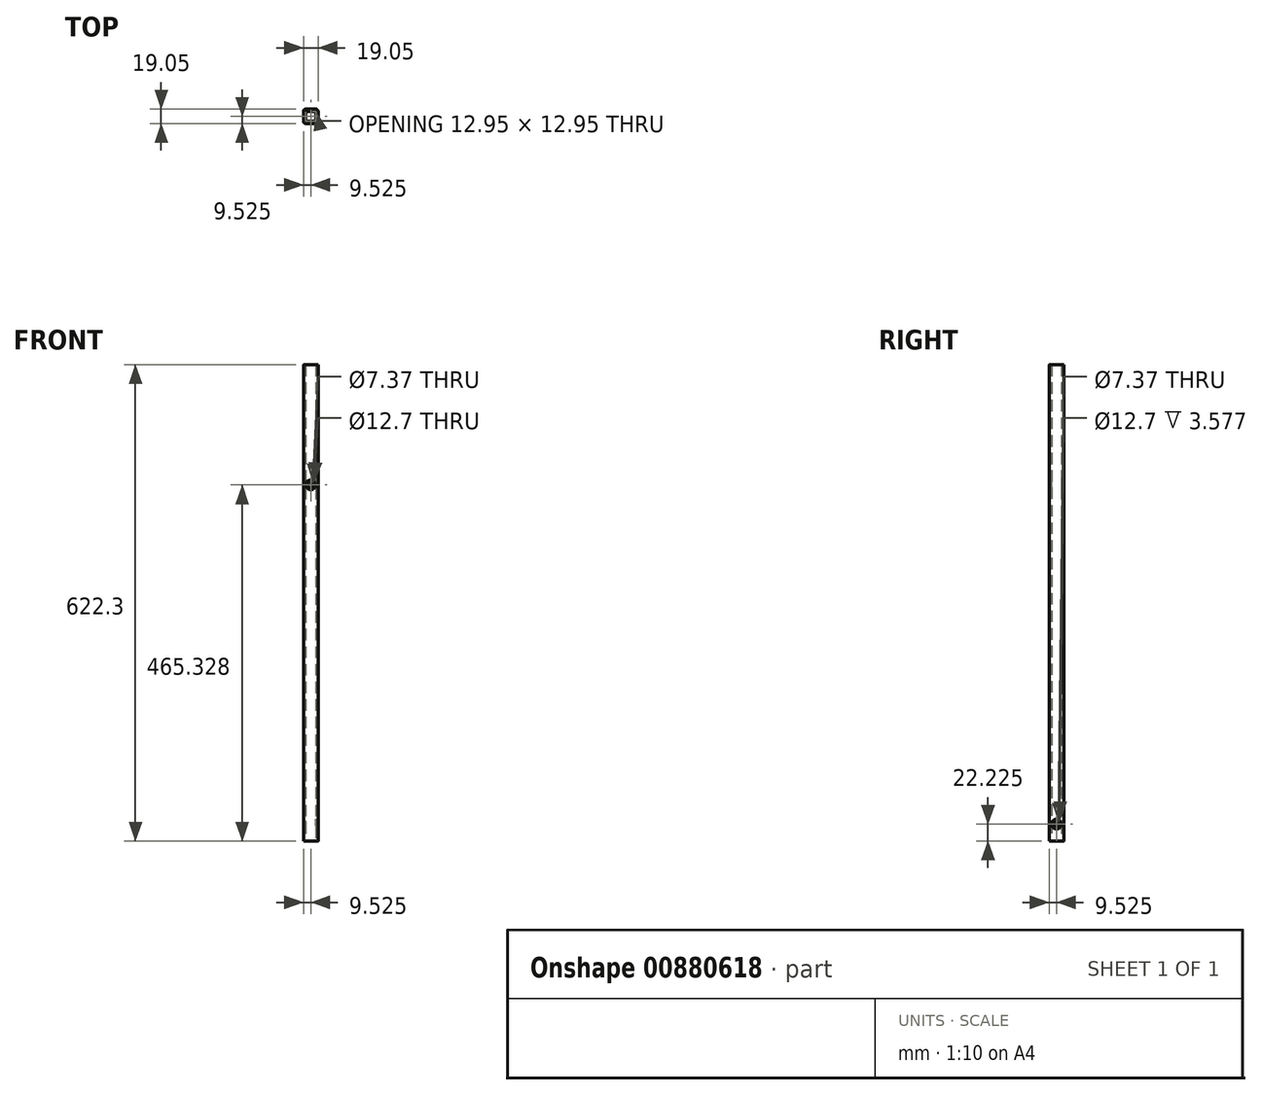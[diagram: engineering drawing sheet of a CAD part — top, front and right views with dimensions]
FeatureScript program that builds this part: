
annotation { "Feature Type Name" : "Feature", "Feature Type Description" : "" }
export const myFeature = defineFeature(function(context is Context, id is Id, definition is map)
    precondition{}
    {
        {
            var Q0;
            Q0=qCreatedBy(makeId("Top.planeOp"),FACE);
            var sketch = newSketch(context, id + "F0", { "sketchPlane" : qUnion([Q0])});
            skLineSegment(sketch, "E0.bottom", {"start": v(3.18, 0) * mm, "end": v(15.87, 0) * mm});
            skLineSegment(sketch, "E0.top", {"start": v(3.18, 19.05) * mm, "end": v(15.88, 19.05) * mm});
            skLineSegment(sketch, "E0.left", {"start": v(0, 3.18) * mm, "end": v(0, 15.87) * mm});
            skLineSegment(sketch, "E0.right", {"start": v(19.05, 3.18) * mm, "end": v(19.05, 15.87) * mm});
            skLineSegment(sketch, "E1.0", {"start": v(4.06, 16) * mm, "end": v(14.99, 16) * mm});
            skLineSegment(sketch, "E1.1", {"start": v(3.05, 4.06) * mm, "end": v(3.05, 14.99) * mm});
            skLineSegment(sketch, "E1.2", {"start": v(4.06, 3.05) * mm, "end": v(14.99, 3.05) * mm});
            skLineSegment(sketch, "E1.3", {"start": v(16, 4.06) * mm, "end": v(16, 14.99) * mm});
            skPoint(sketch, "E2.visualSharp", {"position": v(19.05, 19.05) * mm});
            skArc(sketch, "E2.filletArc", {"start": v(19.05, 15.88) * mm, "mid": v(18.12, 18.12) * mm, "end": v(15.88, 19.05) * mm});
            skPoint(sketch, "E3.visualSharp", {"position": v(19.05, 0) * mm});
            skArc(sketch, "E3.filletArc", {"start": v(15.87, 0) * mm, "mid": v(18.12, 0.93) * mm, "end": v(19.05, 3.18) * mm});
            skPoint(sketch, "E4.visualSharp", {"position": v(0, 0) * mm});
            skArc(sketch, "E4.filletArc", {"start": v(0, 3.17) * mm, "mid": v(0.93, 0.93) * mm, "end": v(3.18, 0) * mm});
            skPoint(sketch, "E5.visualSharp", {"position": v(0, 19.05) * mm});
            skArc(sketch, "E5.filletArc", {"start": v(3.18, 19.05) * mm, "mid": v(0.93, 18.12) * mm, "end": v(0, 15.88) * mm});
            skPoint(sketch, "E6.visualSharp", {"position": v(3.05, 16) * mm});
            skArc(sketch, "E6.filletArc", {"start": v(4.06, 16) * mm, "mid": v(3.35, 15.7) * mm, "end": v(3.05, 14.99) * mm});
            skPoint(sketch, "E7.visualSharp", {"position": v(16, 3.05) * mm});
            skArc(sketch, "E7.filletArc", {"start": v(14.99, 3.05) * mm, "mid": v(15.7, 3.35) * mm, "end": v(16, 4.06) * mm});
            skPoint(sketch, "E8.visualSharp", {"position": v(3.05, 3.05) * mm});
            skArc(sketch, "E8.filletArc", {"start": v(3.05, 4.06) * mm, "mid": v(3.35, 3.35) * mm, "end": v(4.06, 3.05) * mm});
            skPoint(sketch, "E9.visualSharp", {"position": v(16, 16) * mm});
            skArc(sketch, "E9.filletArc", {"start": v(16, 14.99) * mm, "mid": v(15.7, 15.7) * mm, "end": v(14.99, 16) * mm});
            skSolve(sketch);
        }
        {
            var Q0;
            Q0=qSketchRegion(id+"F0",true);
            extrude(context, id + "F1", {"entities" : qUnion([Q0]), "depth" : 622.3 * mm, "offsetDistance" : 25.4 * mm});
        }
        {
            var Q0;
            Q0=qCreatedBy(makeId("Right.planeOp"),FACE);
            var sketch = newSketch(context, id + "F2", { "sketchPlane" : qUnion([Q0])});
            skCircle(sketch, "E10", {"center": v(9.53, 22.23) * mm, "radius": 3.68 * mm});
            skLineSegment(sketch, "E11", {"start": v(0, 22.23) * mm, "end": v(19.05, 22.23) * mm, "construction": true});
            skSolve(sketch);
        }
        {
            var Q0;
            Q0=makeQuery(id+"F2.imprint","IMPRINT",FACE,{"disambiguationData":[TD([[makeQuery(id+"F2.imprint","IMPRINT",EDGE,{"derivedFrom":sQuery(id+"F2.wireOp",EDGE,"E10")}),1.0]])]});
            var Q1;
            Q1=sQuery(id+"F2.wireOp",EDGE,"E10");
            extrude(context, id + "F3", {"entities" : qUnion([Q0]), "operationType" : NewBodyOperationType.REMOVE, "surfaceEntities" : qUnion([Q1]), "depth" : 47.5 * mm, "offsetDistance" : 25.4 * mm});
        }
        {
            var Q0;
            Q0=makeQuery(id+"F1.opExtrude","SWEPT_FACE",FACE,{"disambiguationData":[OSD([sQuery(id+"F0.wireOp",EDGE,"E0.right")])]});
            var sketch = newSketch(context, id + "F4", { "sketchPlane" : qUnion([Q0])});
            skCircle(sketch, "E12", {"center": v(9.53, 22.23) * mm, "radius": 6.35 * mm});
            skSolve(sketch);
        }
        {
            var Q0;
            Q0=qSketchRegion(id+"F4",true);
            extrude(context, id + "F5", {"entities" : qUnion([Q0]), "operationType" : NewBodyOperationType.REMOVE, "oppositeDirection" : true, "depth" : 4.06 * mm, "offsetDistance" : 25.4 * mm});
        }
        {
            var Q0;
            Q0=qCreatedBy(makeId("Front.planeOp"),FACE);
            var sketch = newSketch(context, id + "F6", { "sketchPlane" : qUnion([Q0])});
            skCircle(sketch, "E13", {"center": v(9.53, 465.33) * mm, "radius": 3.68 * mm});
            skLineSegment(sketch, "E14", {"start": v(9.53, 465.33) * mm, "end": v(0, 465.33) * mm, "construction": true});
            skLineSegment(sketch, "E15", {"start": v(9.53, 465.33) * mm, "end": v(19.05, 465.33) * mm, "construction": true});
            skSolve(sketch);
        }
        {
            var Q0;
            Q0=qSketchRegion(id+"F6",true);
            extrude(context, id + "F7", {"entities" : qUnion([Q0]), "operationType" : NewBodyOperationType.REMOVE, "oppositeDirection" : true, "depth" : 25.4 * mm, "offsetDistance" : 25.4 * mm});
        }
        {
            var Q0;
            Q0=makeQuery(id+"F1.opExtrude","SWEPT_FACE",FACE,{"disambiguationData":[OSD([sQuery(id+"F0.wireOp",EDGE,"E0.bottom")])]});
            var sketch = newSketch(context, id + "F8", { "sketchPlane" : qUnion([Q0])});
            skCircle(sketch, "E16", {"center": v(9.53, 465.33) * mm, "radius": 6.35 * mm});
            skSolve(sketch);
        }
        {
            var Q0;
            Q0=qSketchRegion(id+"F8",true);
            extrude(context, id + "F9", {"entities" : qUnion([Q0]), "operationType" : NewBodyOperationType.REMOVE, "oppositeDirection" : true, "depth" : 8.64 * mm, "offsetDistance" : 25.4 * mm});
        }
    });
